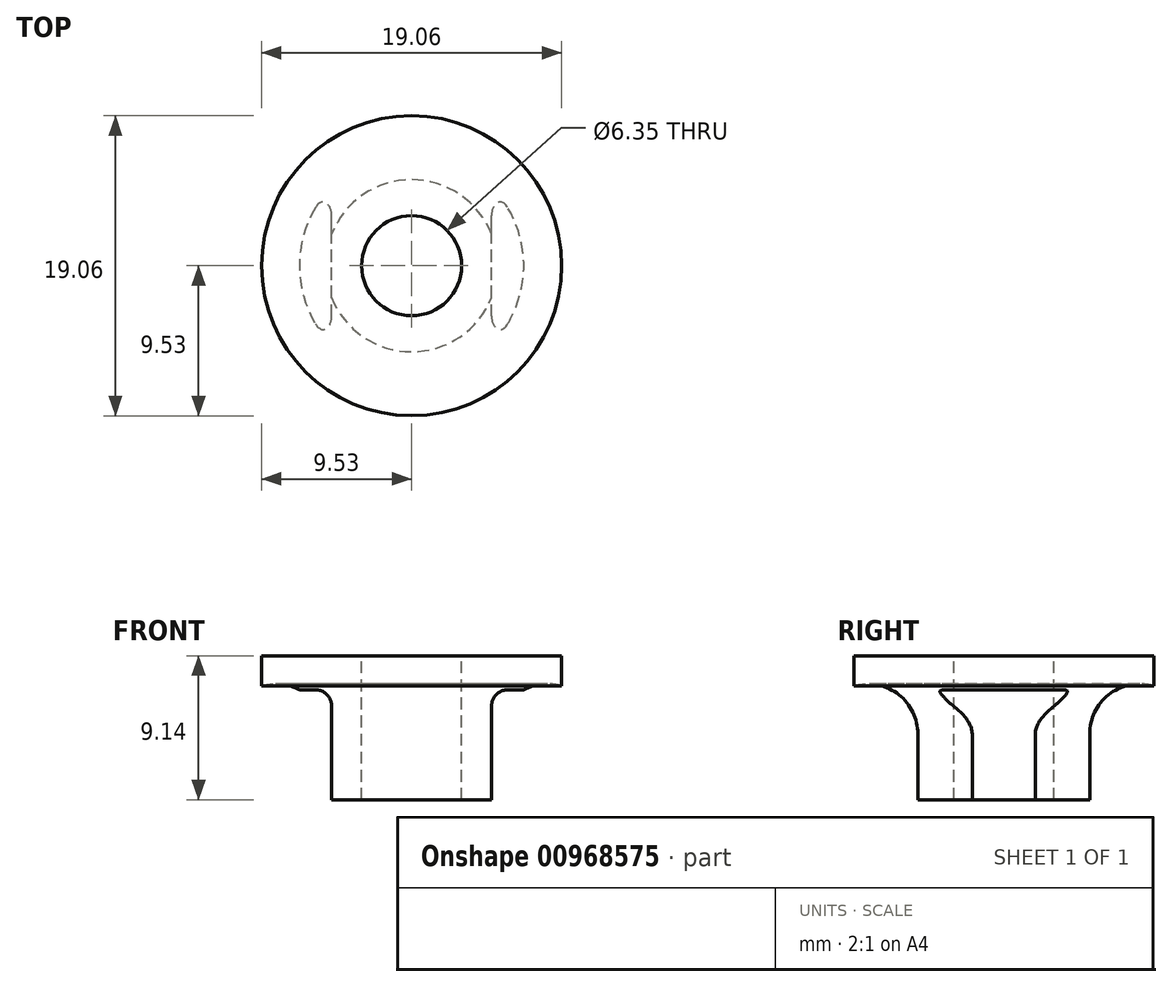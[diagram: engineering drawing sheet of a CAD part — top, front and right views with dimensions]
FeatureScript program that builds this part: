
annotation { "Feature Type Name" : "Feature", "Feature Type Description" : "" }
export const myFeature = defineFeature(function(context is Context, id is Id, definition is map)
    precondition{}
    {
        {
            var Q0;
            Q0=qCreatedBy(makeId("Top.planeOp"),FACE);
            var sketch = newSketch(context, id + "F0", { "sketchPlane" : qUnion([Q0])});
            skCircle(sketch, "E0", {"center": v(0, 0) * mm, "radius": 3.18 * mm});
            skCircle(sketch, "E1", {"center": v(0, 0) * mm, "radius": 9.53 * mm});
            skSolve(sketch);
        }
        {
            var Q0;
            Q0=makeQuery(id+"F0.imprint","IMPRINT",FACE,{"disambiguationData":[TD([[makeQuery(id+"F0.imprint","IMPRINT",EDGE,{"derivedFrom":sQuery(id+"F0.wireOp",EDGE,"E0")}),-1.0]])]});
            extrude(context, id + "F1", {"entities" : qUnion([Q0]), "oppositeDirection" : true, "depth" : 25.4 * mm, "offsetDistance" : 25.4 * mm});
        }
        {
            var Q0;
            Q0=qCreatedBy(makeId("Front.planeOp"),FACE);
            var sketch = newSketch(context, id + "F2", { "sketchPlane" : qUnion([Q0])});
            skLineSegment(sketch, "E2", {"start": v(-8.22, 0) * mm, "end": v(8.35, 0) * mm});
            skCircle(sketch, "E3", {"center": v(8.64, -4.95) * mm, "radius": 3.18 * mm});
            skLineSegment(sketch, "E4", {"start": v(3.18, 0) * mm, "end": v(3.18, -25.4) * mm, "construction": true});
            skLineSegment(sketch, "E5", {"start": v(-3.18, -25.4) * mm, "end": v(-3.18, 0) * mm, "construction": true});
            skLineSegment(sketch, "E6.bottom", {"start": v(12.06, -9.14) * mm, "end": v(0, -9.14) * mm});
            skLineSegment(sketch, "E6.top", {"start": v(12.06, -34.54) * mm, "end": v(0, -34.54) * mm});
            skLineSegment(sketch, "E6.left", {"start": v(12.06, -9.14) * mm, "end": v(12.06, -34.54) * mm});
            skLineSegment(sketch, "E6.right", {"start": v(0, -9.14) * mm, "end": v(0, -34.54) * mm});
            skLineSegment(sketch, "E7.bottom", {"start": v(5.46, -4.95) * mm, "end": v(11.06, -4.95) * mm});
            skLineSegment(sketch, "E7.top", {"start": v(5.46, -9.96) * mm, "end": v(11.06, -9.96) * mm});
            skLineSegment(sketch, "E7.left", {"start": v(5.46, -4.95) * mm, "end": v(5.46, -9.96) * mm});
            skLineSegment(sketch, "E7.right", {"start": v(11.06, -4.95) * mm, "end": v(11.06, -9.96) * mm});
            skSolve(sketch);
        }
        {
            var Q0;
            Q0=makeQuery(id+"F2.imprint","IMPRINT",FACE,{"disambiguationData":[TD([[makeQuery(id+"F2.imprint","IMPRINT",EDGE,{"derivedFrom":sQuery(id+"F2.wireOp",EDGE,"E3")}),1.0]])]});
            var Q1;
            {var subQ1=sQuery(id+"F2.wireOp",EDGE,"E6.top");Q1=makeQuery(id+"F2.imprint","IMPRINT",FACE,{"disambiguationData":[TD([[makeQuery(id+"F2.imprint","IMPRINT",EDGE,{"derivedFrom":subQ1}),-1.0]])]});}
            var Q2;
            {var subQ3=sQuery(id+"F2.wireOp",EDGE,"E7.right");var subQ5=sQuery(id+"F2.wireOp",EDGE,"E6.bottom");var subQ7=makeQuery(id+"F2.imprint","INTERSECT",VERTEX,{"derivedFrom":[subQ5,subQ3]});Q2=makeQuery(id+"F2.imprint","IMPRINT",FACE,{"disambiguationData":[TD([[makeQuery(id+"F2.imprint","IMPRINT",EDGE,{"disambiguationData":[TD([[subQ7,-1.0]])],"derivedFrom":subQ5}),-1.0]])]});}
            var Q3;
            {var subQ5=sQuery(id+"F2.wireOp",EDGE,"E7.top");Q3=makeQuery(id+"F2.imprint","IMPRINT",FACE,{"disambiguationData":[TD([[makeQuery(id+"F2.imprint","IMPRINT",EDGE,{"derivedFrom":subQ5}),1.0]])]});}
            var Q4;
            Q4=makeQuery(id+"F1.opExtrude","CAP_EDGE",EDGE,{"disambiguationData":[OSD([sQuery(id+"F0.wireOp",EDGE,"E1")])],"isStart":false});
            revolve(context, id + "F3", {"operationType" : NewBodyOperationType.REMOVE, "surfaceOperationType" : NewSurfaceOperationType.NEW, "entities" : qUnion([Q0, Q1, Q2, Q3]), "axis" : qUnion([Q4]), "revolveType" : RevolveType.FULL, "oppositeDirection" : true});
        }
        {
            var Q0;
            Q0=makeQuery(id+"F3.boolean.opBoolean","COPY",FACE,{"derivedFrom":makeQuery(id+"F3.opRevolve","SWEPT_FACE",FACE,{"disambiguationData":[OSD([sQuery(id+"F2.wireOp",EDGE,"E6.bottom")])]})});
            var sketch = newSketch(context, id + "F4", { "sketchPlane" : qUnion([Q0])});
            skLineSegment(sketch, "E8.bottom", {"start": v(5.46, 0) * mm, "end": v(11.35, 0) * mm});
            skLineSegment(sketch, "E8.top", {"start": v(5.46, 10.7) * mm, "end": v(11.35, 10.7) * mm});
            skLineSegment(sketch, "E8.left", {"start": v(5.46, 0) * mm, "end": v(5.46, 10.7) * mm});
            skLineSegment(sketch, "E8.right", {"start": v(11.35, 0) * mm, "end": v(11.35, 10.7) * mm});
            skLineSegment(sketch, "E9.bottom", {"start": v(5.46, 0) * mm, "end": v(11.6, 0) * mm});
            skLineSegment(sketch, "E9.top", {"start": v(5.46, -9.42) * mm, "end": v(11.6, -9.42) * mm});
            skLineSegment(sketch, "E9.left", {"start": v(5.46, 0) * mm, "end": v(5.46, -9.42) * mm});
            skLineSegment(sketch, "E9.right", {"start": v(11.6, 0) * mm, "end": v(11.6, -9.42) * mm});
            skLineSegment(sketch, "E10.bottom", {"start": v(-5.46, 0) * mm, "end": v(-11.2, 0) * mm});
            skLineSegment(sketch, "E10.top", {"start": v(-5.46, -10.45) * mm, "end": v(-11.2, -10.45) * mm});
            skLineSegment(sketch, "E10.left", {"start": v(-5.46, 0) * mm, "end": v(-5.46, -10.45) * mm});
            skLineSegment(sketch, "E10.right", {"start": v(-11.2, 0) * mm, "end": v(-11.2, -10.45) * mm});
            skLineSegment(sketch, "E11.top", {"start": v(-5.46, 14.2) * mm, "end": v(-11.2, 14.2) * mm});
            skLineSegment(sketch, "E11.left", {"start": v(-5.46, 0) * mm, "end": v(-5.46, 14.2) * mm});
            skLineSegment(sketch, "E11.right", {"start": v(-11.2, 0) * mm, "end": v(-11.2, 14.2) * mm});
            skLineSegment(sketch, "E12.bottom", {"start": v(5.46, 10.7) * mm, "end": v(5.08, 10.7) * mm});
            skLineSegment(sketch, "E12.top", {"start": v(5.46, -9.07) * mm, "end": v(5.08, -9.07) * mm});
            skLineSegment(sketch, "E12.left", {"start": v(5.46, 10.7) * mm, "end": v(5.46, -9.07) * mm});
            skLineSegment(sketch, "E12.right", {"start": v(5.08, 10.7) * mm, "end": v(5.08, -9.07) * mm});
            skLineSegment(sketch, "E13.bottom", {"start": v(-5.46, 14.2) * mm, "end": v(-5.08, 14.2) * mm});
            skLineSegment(sketch, "E13.top", {"start": v(-5.46, -11.27) * mm, "end": v(-5.08, -11.27) * mm});
            skLineSegment(sketch, "E13.left", {"start": v(-5.46, 14.2) * mm, "end": v(-5.46, -11.27) * mm});
            skLineSegment(sketch, "E13.right", {"start": v(-5.08, 14.2) * mm, "end": v(-5.08, -11.27) * mm});
            skSolve(sketch);
        }
        {
            var Q0;
            Q0=makeQuery(id+"F4.imprint","IMPRINT",FACE,{"disambiguationData":[TD([[makeQuery(id+"F4.imprint","IMPRINT",EDGE,{"derivedFrom":sQuery(id+"F4.wireOp",EDGE,"E10.bottom")}),1.0]])]});
            var Q1;
            Q1=makeQuery(id+"F4.imprint","IMPRINT",FACE,{"disambiguationData":[TD([[makeQuery(id+"F4.imprint","IMPRINT",EDGE,{"derivedFrom":sQuery(id+"F4.wireOp",EDGE,"E10.bottom")}),-1.0]])]});
            var Q2;
            Q2=makeQuery(id+"F4.imprint","IMPRINT",FACE,{"disambiguationData":[TD([[makeQuery(id+"F4.imprint","IMPRINT",EDGE,{"derivedFrom":sQuery(id+"F4.wireOp",EDGE,"E8.bottom")}),1.0]])]});
            var Q3;
            {var subQ1=sQuery(id+"F4.wireOp",EDGE,"E8.bottom");Q3=makeQuery(id+"F4.imprint","IMPRINT",FACE,{"disambiguationData":[TD([[makeQuery(id+"F4.imprint","IMPRINT",EDGE,{"derivedFrom":subQ1}),-1.0]])]});}
            var Q4;
            {var subQ0=sQuery(id+"F4.wireOp",EDGE,"E13.right");var subQ1=makeQuery(id+"F3.boolean.opBoolean","COPY",EDGE,{"derivedFrom":makeQuery(id+"F3.opRevolve","SWEPT_EDGE",EDGE,{"disambiguationData":[OSD([sQuery(id+"F2.wireOp",EDGE,"E6.bottom"),sQuery(id+"F2.wireOp",EDGE,"E7.left")])]})});var subQ2=makeQuery(id+"F4.imprint","INTERSECT",VERTEX,{"disambiguationData":[OD(0.0)],"derivedFrom":[subQ1,subQ0]});Q4=makeQuery(id+"F4.imprint","IMPRINT",FACE,{"disambiguationData":[TD([[makeQuery(id+"F4.imprint","IMPRINT",EDGE,{"disambiguationData":[TD([[subQ2,-1.0]])],"derivedFrom":subQ0}),-1.0]])]});}
            var Q5;
            {var subQ0=sQuery(id+"F4.wireOp",EDGE,"E11.left");Q5=makeQuery(id+"F4.imprint","IMPRINT",FACE,{"disambiguationData":[TD([[makeQuery(id+"F4.imprint","IMPRINT",EDGE,{"derivedFrom":subQ0}),-1.0]])]});}
            var Q6;
            {var subQ1=sQuery(id+"F4.wireOp",EDGE,"E10.left");Q6=makeQuery(id+"F4.imprint","IMPRINT",FACE,{"disambiguationData":[TD([[makeQuery(id+"F4.imprint","IMPRINT",EDGE,{"derivedFrom":subQ1}),1.0]])]});}
            var Q7;
            {var subQ3=sQuery(id+"F4.wireOp",EDGE,"E12.top");Q7=makeQuery(id+"F4.imprint","IMPRINT",FACE,{"disambiguationData":[TD([[makeQuery(id+"F4.imprint","IMPRINT",EDGE,{"derivedFrom":subQ3}),-1.0]])]});}
            var Q8;
            {var subQ0=sQuery(id+"F4.wireOp",EDGE,"E12.right");var subQ1=makeQuery(id+"F3.boolean.opBoolean","COPY",EDGE,{"derivedFrom":makeQuery(id+"F3.opRevolve","SWEPT_EDGE",EDGE,{"disambiguationData":[OSD([sQuery(id+"F2.wireOp",EDGE,"E6.bottom"),sQuery(id+"F2.wireOp",EDGE,"E7.left")])]})});var subQ2=makeQuery(id+"F4.imprint","INTERSECT",VERTEX,{"disambiguationData":[OD(0.0)],"derivedFrom":[subQ1,subQ0]});Q8=makeQuery(id+"F4.imprint","IMPRINT",FACE,{"disambiguationData":[TD([[makeQuery(id+"F4.imprint","IMPRINT",EDGE,{"disambiguationData":[TD([[subQ2,-1.0]])],"derivedFrom":subQ0}),1.0]])]});}
            var Q9;
            {var subQ0=sQuery(id+"F4.wireOp",EDGE,"E8.left");Q9=makeQuery(id+"F4.imprint","IMPRINT",FACE,{"disambiguationData":[TD([[makeQuery(id+"F4.imprint","IMPRINT",EDGE,{"derivedFrom":subQ0}),1.0]])]});}
            extrude(context, id + "F5", {"entities" : qUnion([Q0, Q1, Q2, Q3, Q4, Q5, Q6, Q7, Q8, Q9]), "operationType" : NewBodyOperationType.REMOVE, "oppositeDirection" : true, "depth" : 7 * mm, "offsetDistance" : 25.4 * mm});
        }
        {
            var Q0;
            Q0=makeQuery(id+"F5.boolean.opBoolean","COPY",EDGE,{"derivedFrom":makeQuery(id+"F5.opExtrude","CAP_EDGE",EDGE,{"disambiguationData":[OSD([sQuery(id+"F4.wireOp",EDGE,"E12.right")])],"isStart":false})});
            var Q1;
            Q1=makeQuery(id+"F5.boolean.opBoolean","COPY",EDGE,{"derivedFrom":makeQuery(id+"F5.opExtrude","CAP_EDGE",EDGE,{"disambiguationData":[OSD([sQuery(id+"F4.wireOp",EDGE,"E13.right")])],"isStart":false})});
            fillet(context, id + "F6", {"entities" : qUnion([Q0, Q1]), "radius" : 1.02 * mm, "tangentPropagation" : true, "allowEdgeOverflow" : false});
        }
    });
